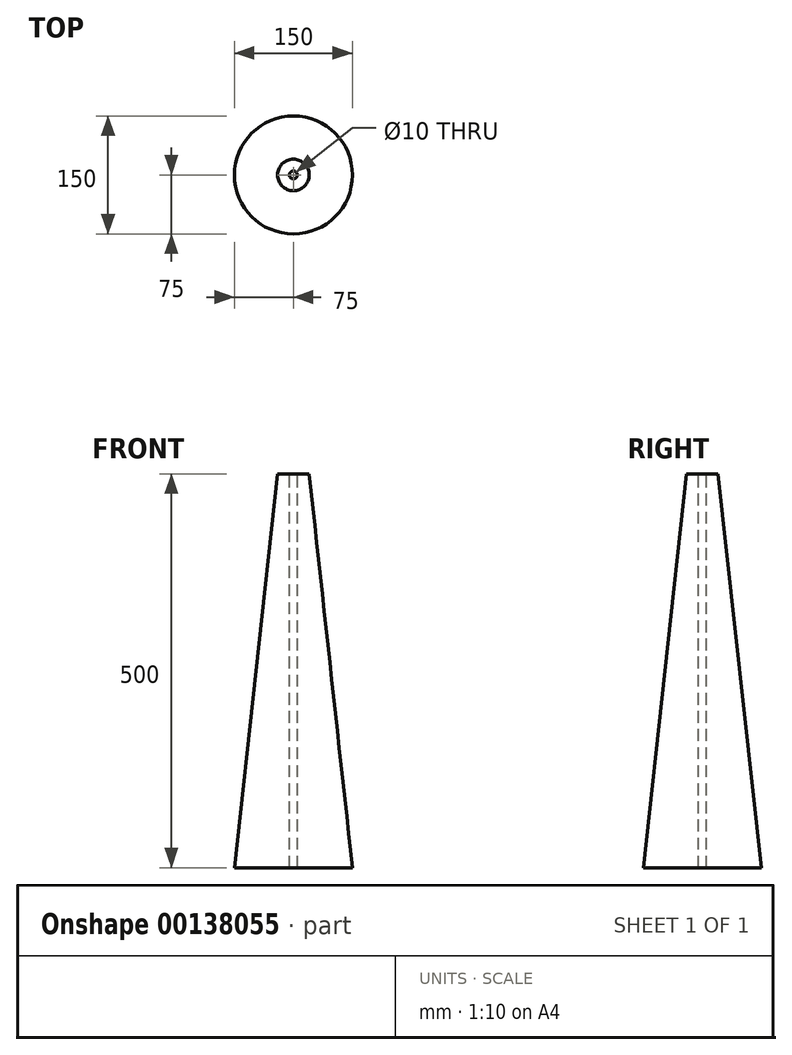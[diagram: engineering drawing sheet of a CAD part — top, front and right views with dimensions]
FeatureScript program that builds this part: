
annotation { "Feature Type Name" : "Feature", "Feature Type Description" : "" }
export const myFeature = defineFeature(function(context is Context, id is Id, definition is map)
    precondition{}
    {
        {
            var Q0;
            Q0=qCreatedBy(makeId("Front.planeOp"),FACE);
            var sketch = newSketch(context, id + "F0", { "sketchPlane" : qUnion([Q0])});
            skLineSegment(sketch, "E0", {"start": v(0, 0) * mm, "end": v(75, 0) * mm});
            skLineSegment(sketch, "E1", {"start": v(75, 0) * mm, "end": v(20, 500) * mm});
            skLineSegment(sketch, "E2", {"start": v(20, 500) * mm, "end": v(0, 500) * mm});
            skLineSegment(sketch, "E3", {"start": v(0, 500) * mm, "end": v(0, 0) * mm});
            skSolve(sketch);
        }
        {
            var Q0;
            Q0=makeQuery(id+"F0.imprint","IMPRINT",FACE,{"disambiguationData":[TD([[makeQuery(id+"F0.imprint","IMPRINT",EDGE,{"derivedFrom":sQuery(id+"F0.wireOp",EDGE,"E0")}),1.0]])]});
            var Q1;
            Q1=sQuery(id+"F0.wireOp",EDGE,"E3");
            revolve(context, id + "F1", {"entities" : qUnion([Q0]), "axis" : qUnion([Q1]), "revolveType" : RevolveType.FULL});
        }
        {
            var Q0;
            Q0=makeQuery(id+"F1.opRevolve","SWEPT_FACE",FACE,{"disambiguationData":[OSD([sQuery(id+"F0.wireOp",EDGE,"E2")])]});
            var sketch = newSketch(context, id + "F2", { "sketchPlane" : qUnion([Q0])});
            skCircle(sketch, "E4", {"center": v(0, 0) * mm, "radius": 5 * mm});
            skSolve(sketch);
        }
        {
            var Q0;
            Q0=makeQuery(id+"F2.imprint","IMPRINT",FACE,{"disambiguationData":[TD([[makeQuery(id+"F2.imprint","IMPRINT",EDGE,{"derivedFrom":sQuery(id+"F2.wireOp",EDGE,"E4")}),1.0]])]});
            extrude(context, id + "F3", {"entities" : qUnion([Q0]), "operationType" : NewBodyOperationType.REMOVE, "endBound" : BoundingType.THROUGH_ALL, "oppositeDirection" : true, "depth" : 25 * mm});
        }
    });
